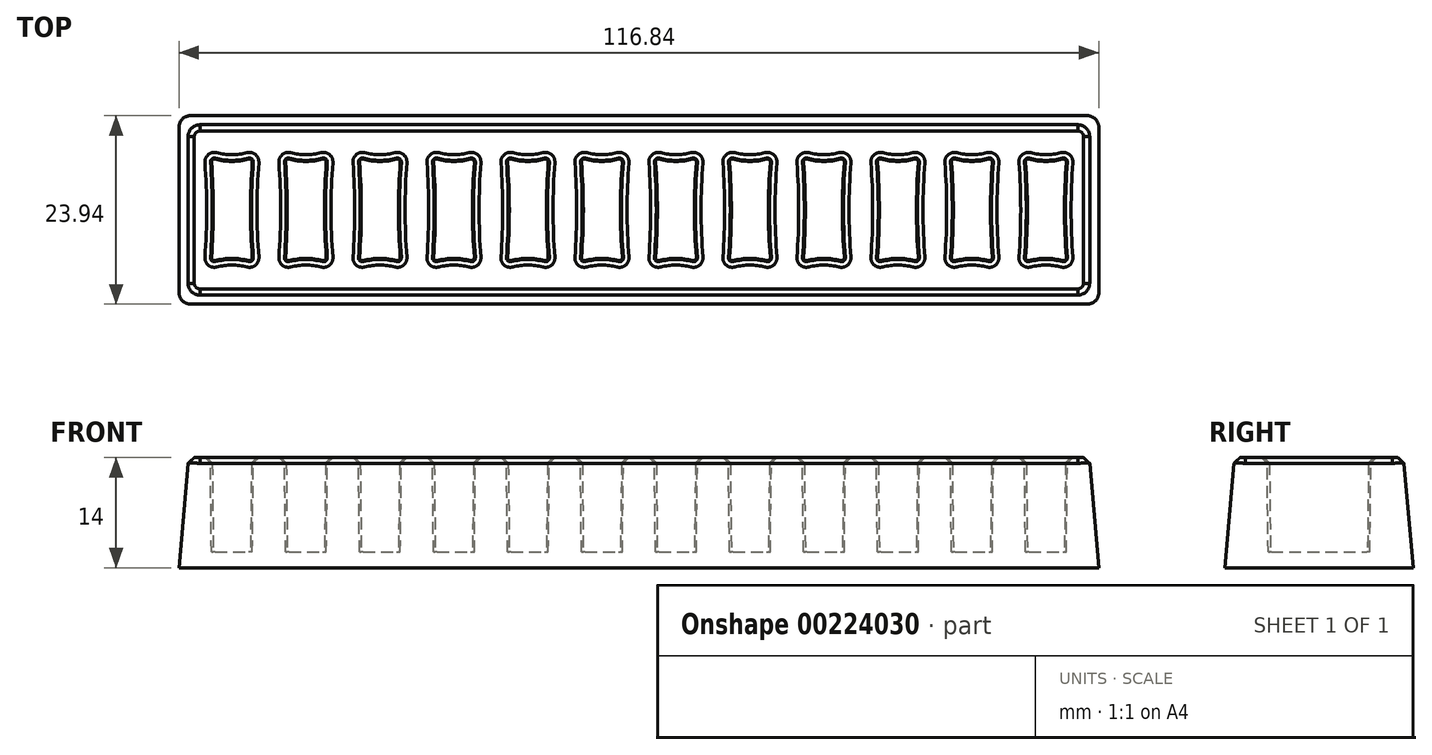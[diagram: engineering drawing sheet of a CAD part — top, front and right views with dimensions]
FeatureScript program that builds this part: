
annotation { "Feature Type Name" : "Feature", "Feature Type Description" : "" }
export const myFeature = defineFeature(function(context is Context, id is Id, definition is map)
    precondition{}
    {
        {
            var Q0;
            Q0=qCreatedBy(makeId("Top.planeOp"),FACE);
            var sketch = newSketch(context, id + "F0", { "sketchPlane" : qUnion([Q0])});
            skLineSegment(sketch, "E0.bottom", {"start": v(0, -10.75) * mm, "end": v(114.4, -10.75) * mm});
            skLineSegment(sketch, "E0.top", {"start": v(0, 10.75) * mm, "end": v(114.4, 10.75) * mm});
            skLineSegment(sketch, "E0.left", {"start": v(0, -10.75) * mm, "end": v(0, 10.75) * mm});
            skLineSegment(sketch, "E0.right", {"start": v(114.4, -10.75) * mm, "end": v(114.4, 10.75) * mm});
            skSolve(sketch);
        }
        {
            var Q0;
            Q0=makeQuery(id+"F0.imprint","IMPRINT",FACE,{"disambiguationData":[TD([[makeQuery(id+"F0.imprint","IMPRINT",EDGE,{"derivedFrom":sQuery(id+"F0.wireOp",EDGE,"E0.bottom")}),1.0]])]});
            var Q1;
            Q1=makeQuery(id+"F0.imprint","IMPRINT",FACE,{"disambiguationData":[TD([[makeQuery(id+"F0.imprint","IMPRINT",EDGE,{"derivedFrom":sQuery(id+"F0.wireOp",EDGE,"ueTfWKIi-SonA-VaYY-VuOx-WjBz5XcDr7Vq.bottom")}),1.0]])]});
            var Q2;
            Q2=makeQuery(id+"F0.imprint","IMPRINT",FACE,{"disambiguationData":[TD([[makeQuery(id+"F0.imprint","IMPRINT",EDGE,{"derivedFrom":sQuery(id+"F0.wireOp",EDGE,"e3a0679b-dacb-468f-a4c3-14299da426ac.1.0.0")}),-1.0]])]});
            var Q3;
            Q3=makeQuery(id+"F0.imprint","IMPRINT",FACE,{"disambiguationData":[TD([[makeQuery(id+"F0.imprint","IMPRINT",EDGE,{"derivedFrom":sQuery(id+"F0.wireOp",EDGE,"e3a0679b-dacb-468f-a4c3-14299da426ac.2.0.0")}),-1.0]])]});
            var Q4;
            Q4=makeQuery(id+"F0.imprint","IMPRINT",FACE,{"disambiguationData":[TD([[makeQuery(id+"F0.imprint","IMPRINT",EDGE,{"derivedFrom":sQuery(id+"F0.wireOp",EDGE,"5b3f68b4-6977-4b90-b81e-3b0594952896.0.3.0")}),-1.0]])]});
            var Q5;
            Q5=makeQuery(id+"F0.imprint","IMPRINT",FACE,{"disambiguationData":[TD([[makeQuery(id+"F0.imprint","IMPRINT",EDGE,{"derivedFrom":sQuery(id+"F0.wireOp",EDGE,"5b3f68b4-6977-4b90-b81e-3b0594952896.0.4.0")}),-1.0]])]});
            var Q6;
            Q6=makeQuery(id+"F0.imprint","IMPRINT",FACE,{"disambiguationData":[TD([[makeQuery(id+"F0.imprint","IMPRINT",EDGE,{"derivedFrom":sQuery(id+"F0.wireOp",EDGE,"5b3f68b4-6977-4b90-b81e-3b0594952896.0.6.0")}),-1.0]])]});
            var Q7;
            Q7=makeQuery(id+"F0.imprint","IMPRINT",FACE,{"disambiguationData":[TD([[makeQuery(id+"F0.imprint","IMPRINT",EDGE,{"derivedFrom":sQuery(id+"F0.wireOp",EDGE,"5b3f68b4-6977-4b90-b81e-3b0594952896.0.7.0")}),-1.0]])]});
            var Q8;
            Q8=makeQuery(id+"F0.imprint","IMPRINT",FACE,{"disambiguationData":[TD([[makeQuery(id+"F0.imprint","IMPRINT",EDGE,{"derivedFrom":sQuery(id+"F0.wireOp",EDGE,"5b3f68b4-6977-4b90-b81e-3b0594952896.0.5.0")}),-1.0]])]});
            var Q9;
            Q9=makeQuery(id+"F0.imprint","IMPRINT",FACE,{"disambiguationData":[TD([[makeQuery(id+"F0.imprint","IMPRINT",EDGE,{"derivedFrom":sQuery(id+"F0.wireOp",EDGE,"7b803989-21a2-4f2c-bcc4-6ed27433c35e.0.8.0")}),-1.0]])]});
            var Q10;
            Q10=makeQuery(id+"F0.imprint","IMPRINT",FACE,{"disambiguationData":[TD([[makeQuery(id+"F0.imprint","IMPRINT",EDGE,{"derivedFrom":sQuery(id+"F0.wireOp",EDGE,"7b803989-21a2-4f2c-bcc4-6ed27433c35e.0.9.0")}),-1.0]])]});
            var Q11;
            Q11=makeQuery(id+"F0.imprint","IMPRINT",FACE,{"disambiguationData":[TD([[makeQuery(id+"F0.imprint","IMPRINT",EDGE,{"derivedFrom":sQuery(id+"F0.wireOp",EDGE,"7b803989-21a2-4f2c-bcc4-6ed27433c35e.0.10.0")}),-1.0]])]});
            var Q12;
            Q12=makeQuery(id+"F0.imprint","IMPRINT",FACE,{"disambiguationData":[TD([[makeQuery(id+"F0.imprint","IMPRINT",EDGE,{"derivedFrom":sQuery(id+"F0.wireOp",EDGE,"7b803989-21a2-4f2c-bcc4-6ed27433c35e.0.11.0")}),-1.0]])]});
            extrude(context, id + "F1", {"entities" : qUnion([Q0, Q1, Q2, Q3, Q4, Q5, Q6, Q7, Q8, Q9, Q10, Q11, Q12]), "oppositeDirection" : true, "offsetDistance" : 25 * mm, "depth" : 14 * mm, "hasDraft" : true, "draftAngle" : 5 * degree});
        }
        {
            var Q0;
            Q0=makeQuery(id+"F1.opExtrude","CAP_FACE",FACE,{"disambiguationData":[OSD([sQuery(id+"F0.wireOp",EDGE,"E0.bottom"),sQuery(id+"F0.wireOp",EDGE,"E0.top"),sQuery(id+"F0.wireOp",EDGE,"E0.left"),sQuery(id+"F0.wireOp",EDGE,"E0.right"),sQuery(id+"F0.wireOp",EDGE,"xGjfcOIm-HSnc-pNGx-gc4Z-AyiedxzzNEQQ"),sQuery(id+"F0.wireOp",EDGE,"YTJknqgt-HmQx-HAe6-ae00-YsNhZU43DuuP"),sQuery(id+"F0.wireOp",EDGE,"M8XJMNeE-EDg2-ARwt-BN1e-G1xgn0dm087A"),sQuery(id+"F0.wireOp",EDGE,"pM8agkuu-0SVb-TDAc-swg6-VZ6Kp682kka8"),sQuery(id+"F0.wireOp",EDGE,"8114b382-a146-4457-b184-7c86869df042.filletArc"),sQuery(id+"F0.wireOp",EDGE,"38438068-d717-4d8c-9960-bff2e024779f.filletArc"),sQuery(id+"F0.wireOp",EDGE,"4a753ca2-9ca1-48ae-85e5-495222f0e263.filletArc"),sQuery(id+"F0.wireOp",EDGE,"6b48d99f-0b37-43ed-b982-f66e7705704f.filletArc")])],"isStart":true});
            var sketch = newSketch(context, id + "F2", { "sketchPlane" : qUnion([Q0])});
            skLineSegment(sketch, "E1.bottom", {"start": v(8, 6.3) * mm, "end": v(3, 6.3) * mm, "construction": true});
            skLineSegment(sketch, "E1.top", {"start": v(8, -6.3) * mm, "end": v(3, -6.3) * mm, "construction": true});
            skLineSegment(sketch, "E1.left", {"start": v(8, 6.3) * mm, "end": v(8, -6.3) * mm, "construction": true});
            skLineSegment(sketch, "E1.right", {"start": v(3, 6.3) * mm, "end": v(3, -6.3) * mm, "construction": true});
            skPoint(sketch, "E1.middle", {"position": v(5.5, 0) * mm});
            skArc(sketch, "E2", {"start": v(3.4, 6.58) * mm, "mid": v(5.5, 6.3) * mm, "end": v(7.6, 6.58) * mm});
            skArc(sketch, "E3", {"start": v(2.77, -6.06) * mm, "mid": v(3, 0) * mm, "end": v(2.77, 6.06) * mm});
            skArc(sketch, "E4", {"start": v(7.6, -6.58) * mm, "mid": v(5.5, -6.3) * mm, "end": v(3.4, -6.58) * mm});
            skArc(sketch, "E5", {"start": v(8.23, 6.06) * mm, "mid": v(8, 0) * mm, "end": v(8.23, -6.06) * mm});
            skPoint(sketch, "E6.visualSharp", {"position": v(2.71, 6.8) * mm});
            skArc(sketch, "E6.filletArc", {"start": v(3.4, 6.58) * mm, "mid": v(2.95, 6.48) * mm, "end": v(2.77, 6.06) * mm});
            skPoint(sketch, "E7.visualSharp", {"position": v(8.29, 6.8) * mm});
            skArc(sketch, "E7.filletArc", {"start": v(8.23, 6.06) * mm, "mid": v(8.05, 6.48) * mm, "end": v(7.6, 6.58) * mm});
            skPoint(sketch, "E8.visualSharp", {"position": v(8.29, -6.8) * mm});
            skArc(sketch, "E8.filletArc", {"start": v(7.6, -6.58) * mm, "mid": v(8.05, -6.48) * mm, "end": v(8.23, -6.06) * mm});
            skPoint(sketch, "E9.visualSharp", {"position": v(2.71, -6.8) * mm});
            skArc(sketch, "E9.filletArc", {"start": v(2.77, -6.06) * mm, "mid": v(2.95, -6.48) * mm, "end": v(3.4, -6.58) * mm});
            skPoint(sketch, "E10.1.0.0", {"position": v(12.11, 6.8) * mm});
            skArc(sketch, "E10.1.0.1", {"start": v(12.8, 6.58) * mm, "mid": v(14.9, 6.3) * mm, "end": v(17, 6.58) * mm});
            skPoint(sketch, "E10.1.0.2", {"position": v(12.11, -6.8) * mm});
            skLineSegment(sketch, "E10.1.0.3", {"start": v(17.4, 6.3) * mm, "end": v(12.4, 6.3) * mm, "construction": true});
            skArc(sketch, "E10.1.0.4", {"start": v(12.17, -6.06) * mm, "mid": v(12.4, 0) * mm, "end": v(12.17, 6.06) * mm});
            skPoint(sketch, "E10.1.0.5", {"position": v(14.9, 0) * mm});
            skLineSegment(sketch, "E10.1.0.6", {"start": v(17.4, 6.3) * mm, "end": v(17.4, -6.3) * mm, "construction": true});
            skLineSegment(sketch, "E10.1.0.7", {"start": v(17.4, -6.3) * mm, "end": v(12.4, -6.3) * mm, "construction": true});
            skLineSegment(sketch, "E10.1.0.8", {"start": v(12.4, 6.3) * mm, "end": v(12.4, -6.3) * mm, "construction": true});
            skPoint(sketch, "E10.1.0.9", {"position": v(17.69, 6.8) * mm});
            skPoint(sketch, "E10.1.0.10", {"position": v(17.69, -6.8) * mm});
            skArc(sketch, "E10.1.0.11", {"start": v(17, -6.58) * mm, "mid": v(14.9, -6.3) * mm, "end": v(12.8, -6.58) * mm});
            skArc(sketch, "E10.1.0.12", {"start": v(17.63, 6.06) * mm, "mid": v(17.4, 0) * mm, "end": v(17.63, -6.06) * mm});
            skPoint(sketch, "E10.1.0.13", {"position": v(14.9, 0) * mm});
            skArc(sketch, "E10.1.0.14", {"start": v(17.63, 6.06) * mm, "mid": v(17.45, 6.48) * mm, "end": v(17, 6.58) * mm});
            skArc(sketch, "E10.1.0.15", {"start": v(12.8, 6.58) * mm, "mid": v(12.35, 6.48) * mm, "end": v(12.17, 6.06) * mm});
            skArc(sketch, "E10.1.0.16", {"start": v(12.17, -6.06) * mm, "mid": v(12.35, -6.48) * mm, "end": v(12.8, -6.58) * mm});
            skArc(sketch, "E10.1.0.17", {"start": v(17, -6.58) * mm, "mid": v(17.45, -6.48) * mm, "end": v(17.63, -6.06) * mm});
            skPoint(sketch, "E10.2.0.0", {"position": v(21.51, 6.8) * mm});
            skArc(sketch, "E10.2.0.1", {"start": v(22.2, 6.58) * mm, "mid": v(24.3, 6.3) * mm, "end": v(26.4, 6.58) * mm});
            skPoint(sketch, "E10.2.0.2", {"position": v(21.51, -6.8) * mm});
            skLineSegment(sketch, "E10.2.0.3", {"start": v(26.8, 6.3) * mm, "end": v(21.8, 6.3) * mm, "construction": true});
            skArc(sketch, "E10.2.0.4", {"start": v(21.57, -6.06) * mm, "mid": v(21.8, 0) * mm, "end": v(21.57, 6.06) * mm});
            skPoint(sketch, "E10.2.0.5", {"position": v(24.3, 0) * mm});
            skLineSegment(sketch, "E10.2.0.6", {"start": v(26.8, 6.3) * mm, "end": v(26.8, -6.3) * mm, "construction": true});
            skLineSegment(sketch, "E10.2.0.7", {"start": v(26.8, -6.3) * mm, "end": v(21.8, -6.3) * mm, "construction": true});
            skLineSegment(sketch, "E10.2.0.8", {"start": v(21.8, 6.3) * mm, "end": v(21.8, -6.3) * mm, "construction": true});
            skPoint(sketch, "E10.2.0.9", {"position": v(27.09, 6.8) * mm});
            skPoint(sketch, "E10.2.0.10", {"position": v(27.09, -6.8) * mm});
            skArc(sketch, "E10.2.0.11", {"start": v(26.4, -6.58) * mm, "mid": v(24.3, -6.3) * mm, "end": v(22.2, -6.58) * mm});
            skArc(sketch, "E10.2.0.12", {"start": v(27.03, 6.06) * mm, "mid": v(26.8, 0) * mm, "end": v(27.03, -6.06) * mm});
            skPoint(sketch, "E10.2.0.13", {"position": v(24.3, 0) * mm});
            skArc(sketch, "E10.2.0.14", {"start": v(27.03, 6.06) * mm, "mid": v(26.85, 6.48) * mm, "end": v(26.4, 6.58) * mm});
            skArc(sketch, "E10.2.0.15", {"start": v(22.2, 6.58) * mm, "mid": v(21.75, 6.48) * mm, "end": v(21.57, 6.06) * mm});
            skArc(sketch, "E10.2.0.16", {"start": v(21.57, -6.06) * mm, "mid": v(21.75, -6.48) * mm, "end": v(22.2, -6.58) * mm});
            skArc(sketch, "E10.2.0.17", {"start": v(26.4, -6.58) * mm, "mid": v(26.85, -6.48) * mm, "end": v(27.03, -6.06) * mm});
            skPoint(sketch, "E10.3.0.0", {"position": v(30.91, 6.8) * mm});
            skArc(sketch, "E10.3.0.1", {"start": v(31.6, 6.58) * mm, "mid": v(33.7, 6.3) * mm, "end": v(35.8, 6.58) * mm});
            skPoint(sketch, "E10.3.0.2", {"position": v(30.91, -6.8) * mm});
            skLineSegment(sketch, "E10.3.0.3", {"start": v(36.2, 6.3) * mm, "end": v(31.2, 6.3) * mm, "construction": true});
            skArc(sketch, "E10.3.0.4", {"start": v(30.97, -6.06) * mm, "mid": v(31.2, 0) * mm, "end": v(30.97, 6.06) * mm});
            skPoint(sketch, "E10.3.0.5", {"position": v(33.7, 0) * mm});
            skLineSegment(sketch, "E10.3.0.6", {"start": v(36.2, 6.3) * mm, "end": v(36.2, -6.3) * mm, "construction": true});
            skLineSegment(sketch, "E10.3.0.7", {"start": v(36.2, -6.3) * mm, "end": v(31.2, -6.3) * mm, "construction": true});
            skLineSegment(sketch, "E10.3.0.8", {"start": v(31.2, 6.3) * mm, "end": v(31.2, -6.3) * mm, "construction": true});
            skPoint(sketch, "E10.3.0.9", {"position": v(36.49, 6.8) * mm});
            skPoint(sketch, "E10.3.0.10", {"position": v(36.49, -6.8) * mm});
            skArc(sketch, "E10.3.0.11", {"start": v(35.8, -6.58) * mm, "mid": v(33.7, -6.3) * mm, "end": v(31.6, -6.58) * mm});
            skArc(sketch, "E10.3.0.12", {"start": v(36.43, 6.06) * mm, "mid": v(36.2, 0) * mm, "end": v(36.43, -6.06) * mm});
            skPoint(sketch, "E10.3.0.13", {"position": v(33.7, 0) * mm});
            skArc(sketch, "E10.3.0.14", {"start": v(36.43, 6.06) * mm, "mid": v(36.25, 6.48) * mm, "end": v(35.8, 6.58) * mm});
            skArc(sketch, "E10.3.0.15", {"start": v(31.6, 6.58) * mm, "mid": v(31.15, 6.48) * mm, "end": v(30.97, 6.06) * mm});
            skArc(sketch, "E10.3.0.16", {"start": v(30.97, -6.06) * mm, "mid": v(31.15, -6.48) * mm, "end": v(31.6, -6.58) * mm});
            skArc(sketch, "E10.3.0.17", {"start": v(35.8, -6.58) * mm, "mid": v(36.25, -6.48) * mm, "end": v(36.43, -6.06) * mm});
            skPoint(sketch, "E10.4.0.0", {"position": v(40.31, 6.8) * mm});
            skArc(sketch, "E10.4.0.1", {"start": v(41, 6.58) * mm, "mid": v(43.1, 6.3) * mm, "end": v(45.2, 6.58) * mm});
            skPoint(sketch, "E10.4.0.2", {"position": v(40.31, -6.8) * mm});
            skLineSegment(sketch, "E10.4.0.3", {"start": v(45.6, 6.3) * mm, "end": v(40.6, 6.3) * mm, "construction": true});
            skArc(sketch, "E10.4.0.4", {"start": v(40.37, -6.06) * mm, "mid": v(40.6, 0) * mm, "end": v(40.37, 6.06) * mm});
            skPoint(sketch, "E10.4.0.5", {"position": v(43.1, 0) * mm});
            skLineSegment(sketch, "E10.4.0.6", {"start": v(45.6, 6.3) * mm, "end": v(45.6, -6.3) * mm, "construction": true});
            skLineSegment(sketch, "E10.4.0.7", {"start": v(45.6, -6.3) * mm, "end": v(40.6, -6.3) * mm, "construction": true});
            skLineSegment(sketch, "E10.4.0.8", {"start": v(40.6, 6.3) * mm, "end": v(40.6, -6.3) * mm, "construction": true});
            skPoint(sketch, "E10.4.0.9", {"position": v(45.89, 6.8) * mm});
            skPoint(sketch, "E10.4.0.10", {"position": v(45.89, -6.8) * mm});
            skArc(sketch, "E10.4.0.11", {"start": v(45.2, -6.58) * mm, "mid": v(43.1, -6.3) * mm, "end": v(41, -6.58) * mm});
            skArc(sketch, "E10.4.0.12", {"start": v(45.83, 6.06) * mm, "mid": v(45.6, 0) * mm, "end": v(45.83, -6.06) * mm});
            skPoint(sketch, "E10.4.0.13", {"position": v(43.1, 0) * mm});
            skArc(sketch, "E10.4.0.14", {"start": v(45.83, 6.06) * mm, "mid": v(45.65, 6.48) * mm, "end": v(45.2, 6.58) * mm});
            skArc(sketch, "E10.4.0.15", {"start": v(41, 6.58) * mm, "mid": v(40.55, 6.48) * mm, "end": v(40.37, 6.06) * mm});
            skArc(sketch, "E10.4.0.16", {"start": v(40.37, -6.06) * mm, "mid": v(40.55, -6.48) * mm, "end": v(41, -6.58) * mm});
            skArc(sketch, "E10.4.0.17", {"start": v(45.2, -6.58) * mm, "mid": v(45.65, -6.48) * mm, "end": v(45.83, -6.06) * mm});
            skPoint(sketch, "E10.5.0.0", {"position": v(49.71, 6.8) * mm});
            skArc(sketch, "E10.5.0.1", {"start": v(50.4, 6.58) * mm, "mid": v(52.5, 6.3) * mm, "end": v(54.6, 6.58) * mm});
            skPoint(sketch, "E10.5.0.2", {"position": v(49.71, -6.8) * mm});
            skLineSegment(sketch, "E10.5.0.3", {"start": v(55, 6.3) * mm, "end": v(50, 6.3) * mm, "construction": true});
            skArc(sketch, "E10.5.0.4", {"start": v(49.77, -6.06) * mm, "mid": v(50, 0) * mm, "end": v(49.77, 6.06) * mm});
            skPoint(sketch, "E10.5.0.5", {"position": v(52.5, 0) * mm});
            skLineSegment(sketch, "E10.5.0.6", {"start": v(55, 6.3) * mm, "end": v(55, -6.3) * mm, "construction": true});
            skLineSegment(sketch, "E10.5.0.7", {"start": v(55, -6.3) * mm, "end": v(50, -6.3) * mm, "construction": true});
            skLineSegment(sketch, "E10.5.0.8", {"start": v(50, 6.3) * mm, "end": v(50, -6.3) * mm, "construction": true});
            skPoint(sketch, "E10.5.0.9", {"position": v(55.29, 6.8) * mm});
            skPoint(sketch, "E10.5.0.10", {"position": v(55.29, -6.8) * mm});
            skArc(sketch, "E10.5.0.11", {"start": v(54.6, -6.58) * mm, "mid": v(52.5, -6.3) * mm, "end": v(50.4, -6.58) * mm});
            skArc(sketch, "E10.5.0.12", {"start": v(55.23, 6.06) * mm, "mid": v(55, 0) * mm, "end": v(55.23, -6.06) * mm});
            skPoint(sketch, "E10.5.0.13", {"position": v(52.5, 0) * mm});
            skArc(sketch, "E10.5.0.14", {"start": v(55.23, 6.06) * mm, "mid": v(55.05, 6.48) * mm, "end": v(54.6, 6.58) * mm});
            skArc(sketch, "E10.5.0.15", {"start": v(50.4, 6.58) * mm, "mid": v(49.95, 6.48) * mm, "end": v(49.77, 6.06) * mm});
            skArc(sketch, "E10.5.0.16", {"start": v(49.77, -6.06) * mm, "mid": v(49.95, -6.48) * mm, "end": v(50.4, -6.58) * mm});
            skArc(sketch, "E10.5.0.17", {"start": v(54.6, -6.58) * mm, "mid": v(55.05, -6.48) * mm, "end": v(55.23, -6.06) * mm});
            skPoint(sketch, "E10.6.0.0", {"position": v(59.11, 6.8) * mm});
            skArc(sketch, "E10.6.0.1", {"start": v(59.8, 6.58) * mm, "mid": v(61.9, 6.3) * mm, "end": v(64, 6.58) * mm});
            skPoint(sketch, "E10.6.0.2", {"position": v(59.11, -6.8) * mm});
            skLineSegment(sketch, "E10.6.0.3", {"start": v(64.4, 6.3) * mm, "end": v(59.4, 6.3) * mm, "construction": true});
            skArc(sketch, "E10.6.0.4", {"start": v(59.17, -6.06) * mm, "mid": v(59.4, 0) * mm, "end": v(59.17, 6.06) * mm});
            skPoint(sketch, "E10.6.0.5", {"position": v(61.9, 0) * mm});
            skLineSegment(sketch, "E10.6.0.6", {"start": v(64.4, 6.3) * mm, "end": v(64.4, -6.3) * mm, "construction": true});
            skLineSegment(sketch, "E10.6.0.7", {"start": v(64.4, -6.3) * mm, "end": v(59.4, -6.3) * mm, "construction": true});
            skLineSegment(sketch, "E10.6.0.8", {"start": v(59.4, 6.3) * mm, "end": v(59.4, -6.3) * mm, "construction": true});
            skPoint(sketch, "E10.6.0.9", {"position": v(64.69, 6.8) * mm});
            skPoint(sketch, "E10.6.0.10", {"position": v(64.69, -6.8) * mm});
            skArc(sketch, "E10.6.0.11", {"start": v(64, -6.58) * mm, "mid": v(61.9, -6.3) * mm, "end": v(59.8, -6.58) * mm});
            skArc(sketch, "E10.6.0.12", {"start": v(64.63, 6.06) * mm, "mid": v(64.4, 0) * mm, "end": v(64.63, -6.06) * mm});
            skPoint(sketch, "E10.6.0.13", {"position": v(61.9, 0) * mm});
            skArc(sketch, "E10.6.0.14", {"start": v(64.63, 6.06) * mm, "mid": v(64.45, 6.48) * mm, "end": v(64, 6.58) * mm});
            skArc(sketch, "E10.6.0.15", {"start": v(59.8, 6.58) * mm, "mid": v(59.35, 6.48) * mm, "end": v(59.17, 6.06) * mm});
            skArc(sketch, "E10.6.0.16", {"start": v(59.17, -6.06) * mm, "mid": v(59.35, -6.48) * mm, "end": v(59.8, -6.58) * mm});
            skArc(sketch, "E10.6.0.17", {"start": v(64, -6.58) * mm, "mid": v(64.45, -6.48) * mm, "end": v(64.63, -6.06) * mm});
            skPoint(sketch, "E10.7.0.0", {"position": v(68.51, 6.8) * mm});
            skArc(sketch, "E10.7.0.1", {"start": v(69.2, 6.58) * mm, "mid": v(71.3, 6.3) * mm, "end": v(73.4, 6.58) * mm});
            skPoint(sketch, "E10.7.0.2", {"position": v(68.51, -6.8) * mm});
            skLineSegment(sketch, "E10.7.0.3", {"start": v(73.8, 6.3) * mm, "end": v(68.8, 6.3) * mm, "construction": true});
            skArc(sketch, "E10.7.0.4", {"start": v(68.57, -6.06) * mm, "mid": v(68.8, 0) * mm, "end": v(68.57, 6.06) * mm});
            skPoint(sketch, "E10.7.0.5", {"position": v(71.3, 0) * mm});
            skLineSegment(sketch, "E10.7.0.6", {"start": v(73.8, 6.3) * mm, "end": v(73.8, -6.3) * mm, "construction": true});
            skLineSegment(sketch, "E10.7.0.7", {"start": v(73.8, -6.3) * mm, "end": v(68.8, -6.3) * mm, "construction": true});
            skLineSegment(sketch, "E10.7.0.8", {"start": v(68.8, 6.3) * mm, "end": v(68.8, -6.3) * mm, "construction": true});
            skPoint(sketch, "E10.7.0.9", {"position": v(74.09, 6.8) * mm});
            skPoint(sketch, "E10.7.0.10", {"position": v(74.09, -6.8) * mm});
            skArc(sketch, "E10.7.0.11", {"start": v(73.4, -6.58) * mm, "mid": v(71.3, -6.3) * mm, "end": v(69.2, -6.58) * mm});
            skArc(sketch, "E10.7.0.12", {"start": v(74.03, 6.06) * mm, "mid": v(73.8, 0) * mm, "end": v(74.03, -6.06) * mm});
            skPoint(sketch, "E10.7.0.13", {"position": v(71.3, 0) * mm});
            skArc(sketch, "E10.7.0.14", {"start": v(74.03, 6.06) * mm, "mid": v(73.85, 6.48) * mm, "end": v(73.4, 6.58) * mm});
            skArc(sketch, "E10.7.0.15", {"start": v(69.2, 6.58) * mm, "mid": v(68.75, 6.48) * mm, "end": v(68.57, 6.06) * mm});
            skArc(sketch, "E10.7.0.16", {"start": v(68.57, -6.06) * mm, "mid": v(68.75, -6.48) * mm, "end": v(69.2, -6.58) * mm});
            skArc(sketch, "E10.7.0.17", {"start": v(73.4, -6.58) * mm, "mid": v(73.85, -6.48) * mm, "end": v(74.03, -6.06) * mm});
            skPoint(sketch, "E10.8.0.0", {"position": v(77.91, 6.8) * mm});
            skArc(sketch, "E10.8.0.1", {"start": v(78.6, 6.58) * mm, "mid": v(80.7, 6.3) * mm, "end": v(82.8, 6.58) * mm});
            skPoint(sketch, "E10.8.0.2", {"position": v(77.91, -6.8) * mm});
            skLineSegment(sketch, "E10.8.0.3", {"start": v(83.2, 6.3) * mm, "end": v(78.2, 6.3) * mm, "construction": true});
            skArc(sketch, "E10.8.0.4", {"start": v(77.97, -6.06) * mm, "mid": v(78.2, 0) * mm, "end": v(77.97, 6.06) * mm});
            skPoint(sketch, "E10.8.0.5", {"position": v(80.7, 0) * mm});
            skLineSegment(sketch, "E10.8.0.6", {"start": v(83.2, 6.3) * mm, "end": v(83.2, -6.3) * mm, "construction": true});
            skLineSegment(sketch, "E10.8.0.7", {"start": v(83.2, -6.3) * mm, "end": v(78.2, -6.3) * mm, "construction": true});
            skLineSegment(sketch, "E10.8.0.8", {"start": v(78.2, 6.3) * mm, "end": v(78.2, -6.3) * mm, "construction": true});
            skPoint(sketch, "E10.8.0.9", {"position": v(83.49, 6.8) * mm});
            skPoint(sketch, "E10.8.0.10", {"position": v(83.49, -6.8) * mm});
            skArc(sketch, "E10.8.0.11", {"start": v(82.8, -6.58) * mm, "mid": v(80.7, -6.3) * mm, "end": v(78.6, -6.58) * mm});
            skArc(sketch, "E10.8.0.12", {"start": v(83.43, 6.06) * mm, "mid": v(83.2, 0) * mm, "end": v(83.43, -6.06) * mm});
            skPoint(sketch, "E10.8.0.13", {"position": v(80.7, 0) * mm});
            skArc(sketch, "E10.8.0.14", {"start": v(83.43, 6.06) * mm, "mid": v(83.25, 6.48) * mm, "end": v(82.8, 6.58) * mm});
            skArc(sketch, "E10.8.0.15", {"start": v(78.6, 6.58) * mm, "mid": v(78.15, 6.48) * mm, "end": v(77.97, 6.06) * mm});
            skArc(sketch, "E10.8.0.16", {"start": v(77.97, -6.06) * mm, "mid": v(78.15, -6.48) * mm, "end": v(78.6, -6.58) * mm});
            skArc(sketch, "E10.8.0.17", {"start": v(82.8, -6.58) * mm, "mid": v(83.25, -6.48) * mm, "end": v(83.43, -6.06) * mm});
            skPoint(sketch, "E10.9.0.0", {"position": v(87.31, 6.8) * mm});
            skArc(sketch, "E10.9.0.1", {"start": v(88, 6.58) * mm, "mid": v(90.1, 6.3) * mm, "end": v(92.2, 6.58) * mm});
            skPoint(sketch, "E10.9.0.2", {"position": v(87.31, -6.8) * mm});
            skLineSegment(sketch, "E10.9.0.3", {"start": v(92.6, 6.3) * mm, "end": v(87.6, 6.3) * mm, "construction": true});
            skArc(sketch, "E10.9.0.4", {"start": v(87.37, -6.06) * mm, "mid": v(87.6, 0) * mm, "end": v(87.37, 6.06) * mm});
            skPoint(sketch, "E10.9.0.5", {"position": v(90.1, 0) * mm});
            skLineSegment(sketch, "E10.9.0.6", {"start": v(92.6, 6.3) * mm, "end": v(92.6, -6.3) * mm, "construction": true});
            skLineSegment(sketch, "E10.9.0.7", {"start": v(92.6, -6.3) * mm, "end": v(87.6, -6.3) * mm, "construction": true});
            skLineSegment(sketch, "E10.9.0.8", {"start": v(87.6, 6.3) * mm, "end": v(87.6, -6.3) * mm, "construction": true});
            skPoint(sketch, "E10.9.0.9", {"position": v(92.89, 6.8) * mm});
            skPoint(sketch, "E10.9.0.10", {"position": v(92.89, -6.8) * mm});
            skArc(sketch, "E10.9.0.11", {"start": v(92.2, -6.58) * mm, "mid": v(90.1, -6.3) * mm, "end": v(88, -6.58) * mm});
            skArc(sketch, "E10.9.0.12", {"start": v(92.83, 6.06) * mm, "mid": v(92.6, 0) * mm, "end": v(92.83, -6.06) * mm});
            skPoint(sketch, "E10.9.0.13", {"position": v(90.1, 0) * mm});
            skArc(sketch, "E10.9.0.14", {"start": v(92.83, 6.06) * mm, "mid": v(92.65, 6.48) * mm, "end": v(92.2, 6.58) * mm});
            skArc(sketch, "E10.9.0.15", {"start": v(88, 6.58) * mm, "mid": v(87.55, 6.48) * mm, "end": v(87.37, 6.06) * mm});
            skArc(sketch, "E10.9.0.16", {"start": v(87.37, -6.06) * mm, "mid": v(87.55, -6.48) * mm, "end": v(88, -6.58) * mm});
            skArc(sketch, "E10.9.0.17", {"start": v(92.2, -6.58) * mm, "mid": v(92.65, -6.48) * mm, "end": v(92.83, -6.06) * mm});
            skPoint(sketch, "E10.10.0.0", {"position": v(96.71, 6.8) * mm});
            skArc(sketch, "E10.10.0.1", {"start": v(97.4, 6.58) * mm, "mid": v(99.5, 6.3) * mm, "end": v(101.6, 6.58) * mm});
            skPoint(sketch, "E10.10.0.2", {"position": v(96.71, -6.8) * mm});
            skLineSegment(sketch, "E10.10.0.3", {"start": v(102, 6.3) * mm, "end": v(97, 6.3) * mm, "construction": true});
            skArc(sketch, "E10.10.0.4", {"start": v(96.77, -6.06) * mm, "mid": v(97, 0) * mm, "end": v(96.77, 6.06) * mm});
            skPoint(sketch, "E10.10.0.5", {"position": v(99.5, 0) * mm});
            skLineSegment(sketch, "E10.10.0.6", {"start": v(102, 6.3) * mm, "end": v(102, -6.3) * mm, "construction": true});
            skLineSegment(sketch, "E10.10.0.7", {"start": v(102, -6.3) * mm, "end": v(97, -6.3) * mm, "construction": true});
            skLineSegment(sketch, "E10.10.0.8", {"start": v(97, 6.3) * mm, "end": v(97, -6.3) * mm, "construction": true});
            skPoint(sketch, "E10.10.0.9", {"position": v(102.29, 6.8) * mm});
            skPoint(sketch, "E10.10.0.10", {"position": v(102.29, -6.8) * mm});
            skArc(sketch, "E10.10.0.11", {"start": v(101.6, -6.58) * mm, "mid": v(99.5, -6.3) * mm, "end": v(97.4, -6.58) * mm});
            skArc(sketch, "E10.10.0.12", {"start": v(102.23, 6.06) * mm, "mid": v(102, 0) * mm, "end": v(102.23, -6.06) * mm});
            skPoint(sketch, "E10.10.0.13", {"position": v(99.5, 0) * mm});
            skArc(sketch, "E10.10.0.14", {"start": v(102.23, 6.06) * mm, "mid": v(102.05, 6.48) * mm, "end": v(101.6, 6.58) * mm});
            skArc(sketch, "E10.10.0.15", {"start": v(97.4, 6.58) * mm, "mid": v(96.95, 6.48) * mm, "end": v(96.77, 6.06) * mm});
            skArc(sketch, "E10.10.0.16", {"start": v(96.77, -6.06) * mm, "mid": v(96.95, -6.48) * mm, "end": v(97.4, -6.58) * mm});
            skArc(sketch, "E10.10.0.17", {"start": v(101.6, -6.58) * mm, "mid": v(102.05, -6.48) * mm, "end": v(102.23, -6.06) * mm});
            skPoint(sketch, "E10.11.0.0", {"position": v(106.11, 6.8) * mm});
            skArc(sketch, "E10.11.0.1", {"start": v(106.8, 6.58) * mm, "mid": v(108.9, 6.3) * mm, "end": v(111, 6.58) * mm});
            skPoint(sketch, "E10.11.0.2", {"position": v(106.11, -6.8) * mm});
            skLineSegment(sketch, "E10.11.0.3", {"start": v(111.4, 6.3) * mm, "end": v(106.4, 6.3) * mm, "construction": true});
            skArc(sketch, "E10.11.0.4", {"start": v(106.17, -6.06) * mm, "mid": v(106.4, 0) * mm, "end": v(106.17, 6.06) * mm});
            skPoint(sketch, "E10.11.0.5", {"position": v(108.9, 0) * mm});
            skLineSegment(sketch, "E10.11.0.6", {"start": v(111.4, 6.3) * mm, "end": v(111.4, -6.3) * mm, "construction": true});
            skLineSegment(sketch, "E10.11.0.7", {"start": v(111.4, -6.3) * mm, "end": v(106.4, -6.3) * mm, "construction": true});
            skLineSegment(sketch, "E10.11.0.8", {"start": v(106.4, 6.3) * mm, "end": v(106.4, -6.3) * mm, "construction": true});
            skPoint(sketch, "E10.11.0.9", {"position": v(111.69, 6.8) * mm});
            skPoint(sketch, "E10.11.0.10", {"position": v(111.69, -6.8) * mm});
            skArc(sketch, "E10.11.0.11", {"start": v(111, -6.58) * mm, "mid": v(108.9, -6.3) * mm, "end": v(106.8, -6.58) * mm});
            skArc(sketch, "E10.11.0.12", {"start": v(111.63, 6.06) * mm, "mid": v(111.4, 0) * mm, "end": v(111.63, -6.06) * mm});
            skPoint(sketch, "E10.11.0.13", {"position": v(108.9, 0) * mm});
            skArc(sketch, "E10.11.0.14", {"start": v(111.63, 6.06) * mm, "mid": v(111.45, 6.48) * mm, "end": v(111, 6.58) * mm});
            skArc(sketch, "E10.11.0.15", {"start": v(106.8, 6.58) * mm, "mid": v(106.35, 6.48) * mm, "end": v(106.17, 6.06) * mm});
            skArc(sketch, "E10.11.0.16", {"start": v(106.17, -6.06) * mm, "mid": v(106.35, -6.48) * mm, "end": v(106.8, -6.58) * mm});
            skArc(sketch, "E10.11.0.17", {"start": v(111, -6.58) * mm, "mid": v(111.45, -6.48) * mm, "end": v(111.63, -6.06) * mm});
            skLineSegment(sketch, "E10.direction1", {"start": v(5.5, 0) * mm, "end": v(14.9, 0) * mm, "construction": true});
            skSolve(sketch);
        }
        {
            var Q0;
            Q0 = qSketchRegion(id + "F2", true);
            extrude(context, id + "F3", {"entities" : qUnion([Q0]), "operationType" : NewBodyOperationType.REMOVE, "oppositeDirection" : true, "offsetDistance" : 25 * mm, "depth" : 12 * mm, "hasDraft" : true, "draftAngle" : .66 * degree, "draftPullDirection" : true});
        }
        {
            var Q0;
            Q0=makeQuery(id+"F1.opExtrude","SWEPT_EDGE",EDGE,{"disambiguationData":[OSD([sQuery(id+"F0.wireOp",EDGE,"E0.bottom"),sQuery(id+"F0.wireOp",EDGE,"E0.left")])]});
            var Q1;
            Q1=makeQuery(id+"F1.opExtrude","SWEPT_EDGE",EDGE,{"disambiguationData":[OSD([sQuery(id+"F0.wireOp",EDGE,"E0.top"),sQuery(id+"F0.wireOp",EDGE,"E0.left")])]});
            var Q2;
            Q2=makeQuery(id+"F1.opExtrude","SWEPT_EDGE",EDGE,{"disambiguationData":[OSD([sQuery(id+"F0.wireOp",EDGE,"E0.top"),sQuery(id+"F0.wireOp",EDGE,"E0.right")])]});
            var Q3;
            Q3=makeQuery(id+"F1.opExtrude","SWEPT_EDGE",EDGE,{"disambiguationData":[OSD([sQuery(id+"F0.wireOp",EDGE,"E0.bottom"),sQuery(id+"F0.wireOp",EDGE,"E0.right")])]});
            fillet(context, id + "F4", {"entities" : qUnion([Q0, Q1, Q2, Q3]), "radius" : 1.5 * mm, "tangentPropagation" : true, "allowEdgeOverflow" : false});
        }
        {
            var Q0;
            Q0=makeQuery(id+"F1.opExtrude","CAP_FACE",FACE,{"disambiguationData":[OSD([sQuery(id+"F0.wireOp",EDGE,"E0.bottom"),sQuery(id+"F0.wireOp",EDGE,"E0.top"),sQuery(id+"F0.wireOp",EDGE,"E0.left"),sQuery(id+"F0.wireOp",EDGE,"E0.right")])],"isStart":true});
            chamfer(context, id + "F5", {"entities" : qUnion([Q0]), "width" : .7 * mm, "tangentPropagation" : true});
        }
    });
